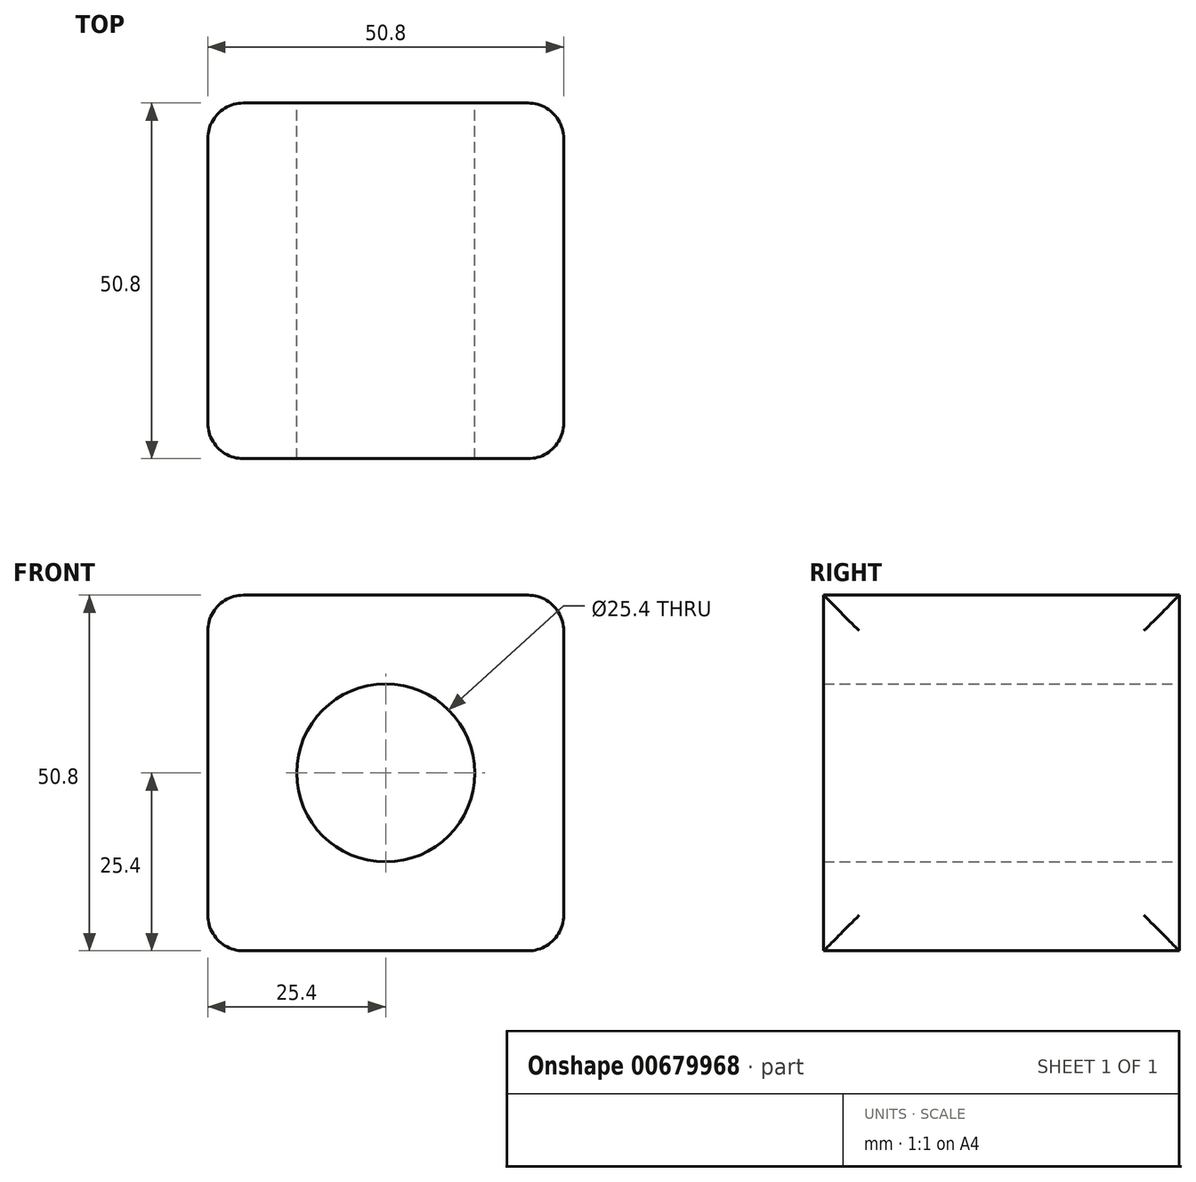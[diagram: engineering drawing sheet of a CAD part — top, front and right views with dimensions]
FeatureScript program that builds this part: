
annotation { "Feature Type Name" : "Feature", "Feature Type Description" : "" }
export const myFeature = defineFeature(function(context is Context, id is Id, definition is map)
    precondition{}
    {
        {
            var Q0;
            Q0=qCreatedBy(makeId("Front.planeOp"),FACE);
            var sketch = newSketch(context, id + "F0", { "sketchPlane" : qUnion([Q0])});
            skLineSegment(sketch, "E0.bottom", {"start": v(0, 0) * mm, "end": v(25.4, 0) * mm});
            skLineSegment(sketch, "E0.top", {"start": v(0, 25.4) * mm, "end": v(25.4, 25.4) * mm});
            skLineSegment(sketch, "E0.left", {"start": v(0, 0) * mm, "end": v(0, 25.4) * mm});
            skLineSegment(sketch, "E0.right", {"start": v(25.4, 0) * mm, "end": v(25.4, 25.4) * mm});
            skLineSegment(sketch, "E1.MirrorCS", {"start": v(0, 25.4) * mm, "end": v(-25.4, 25.4) * mm});
            skLineSegment(sketch, "E2.MirrorCS", {"start": v(-25.4, 0) * mm, "end": v(-25.4, 25.4) * mm});
            skLineSegment(sketch, "E3.MirrorCS", {"start": v(0, -25.4) * mm, "end": v(-25.4, -25.4) * mm});
            skLineSegment(sketch, "E4.MirrorCS", {"start": v(-25.4, 0) * mm, "end": v(-25.4, -25.4) * mm});
            skLineSegment(sketch, "E5.MirrorCS", {"start": v(0, -25.4) * mm, "end": v(25.4, -25.4) * mm});
            skLineSegment(sketch, "E6.MirrorCS", {"start": v(25.4, 0) * mm, "end": v(25.4, -25.4) * mm});
            skCircle(sketch, "E7", {"center": v(0, 0) * mm, "radius": 12.7 * mm});
            skSolve(sketch);
        }
        {
            var Q0;
            {var subQ0=sQuery(id+"F0.wireOp",EDGE,"E1.MirrorCS");Q0=makeQuery(id+"F0.imprint","IMPRINT",FACE,{"disambiguationData":[TD([[makeQuery(id+"F0.imprint","IMPRINT",EDGE,{"derivedFrom":subQ0}),1.0]])]});}
            var Q1;
            {var subQ2=sQuery(id+"F0.wireOp",EDGE,"E0.top");Q1=makeQuery(id+"F0.imprint","IMPRINT",FACE,{"disambiguationData":[TD([[makeQuery(id+"F0.imprint","IMPRINT",EDGE,{"derivedFrom":subQ2}),-1.0]])]});}
            extrude(context, id + "F1", {"entities" : qUnion([Q0, Q1]), "depth" : 50.8 * mm, "offsetDistance" : 25.4 * mm});
        }
        {
            var Q0;
            Q0=sQuery(id+"F0.wireOp",EDGE,"E7");
            extrude(context, id + "F2", {"bodyType" : ToolBodyType.SURFACE, "surfaceEntities" : qUnion([Q0]), "depth" : 101.6 * mm, "offsetDistance" : 25.4 * mm, "hasSecondDirection" : true, "secondDirectionOppositeDirection" : true, "secondDirectionDepth" : 50.8 * mm});
        }
        {
            var Q0;
            Q0=makeQuery(id+"F1.opExtrude","SWEPT_EDGE",EDGE,{"disambiguationData":[OSD([sQuery(id+"F0.wireOp",EDGE,"E1.MirrorCS"),sQuery(id+"F0.wireOp",EDGE,"E2.MirrorCS")])]});
            var Q1;
            Q1=makeQuery(id+"F1.opExtrude","SWEPT_EDGE",EDGE,{"disambiguationData":[OSD([sQuery(id+"F0.wireOp",EDGE,"E0.top"),sQuery(id+"F0.wireOp",EDGE,"E0.right")])]});
            var Q2;
            Q2=makeQuery(id+"F1.opExtrude","SWEPT_EDGE",EDGE,{"disambiguationData":[OSD([sQuery(id+"F0.wireOp",EDGE,"E3.MirrorCS"),sQuery(id+"F0.wireOp",EDGE,"E4.MirrorCS")])]});
            var Q3;
            Q3=makeQuery(id+"F1.opExtrude","SWEPT_EDGE",EDGE,{"disambiguationData":[OSD([sQuery(id+"F0.wireOp",EDGE,"E5.MirrorCS"),sQuery(id+"F0.wireOp",EDGE,"E6.MirrorCS")])]});
            var Q4;
            Q4=makeQuery(id+"F1.opExtrude","CAP_EDGE",EDGE,{"disambiguationData":[OSD([sQuery(id+"F0.wireOp",EDGE,"E0.right"),sQuery(id+"F0.wireOp",EDGE,"E6.MirrorCS")])],"isStart":true});
            var Q5;
            Q5=makeQuery(id+"F1.opExtrude","CAP_EDGE",EDGE,{"disambiguationData":[OSD([sQuery(id+"F0.wireOp",EDGE,"E2.MirrorCS"),sQuery(id+"F0.wireOp",EDGE,"E4.MirrorCS")])],"isStart":true});
            var Q6;
            Q6=makeQuery(id+"F1.opExtrude","CAP_EDGE",EDGE,{"disambiguationData":[OSD([sQuery(id+"F0.wireOp",EDGE,"E2.MirrorCS"),sQuery(id+"F0.wireOp",EDGE,"E4.MirrorCS")])],"isStart":false});
            var Q7;
            Q7=makeQuery(id+"F1.opExtrude","CAP_EDGE",EDGE,{"disambiguationData":[OSD([sQuery(id+"F0.wireOp",EDGE,"E0.right"),sQuery(id+"F0.wireOp",EDGE,"E6.MirrorCS")])],"isStart":false});
            fillet(context, id + "F3", {"entities" : qUnion([Q0, Q1, Q2, Q3, Q4, Q5, Q6, Q7]), "radius" : 5.08 * mm, "tangentPropagation" : true, "allowEdgeOverflow" : false});
        }
    });
